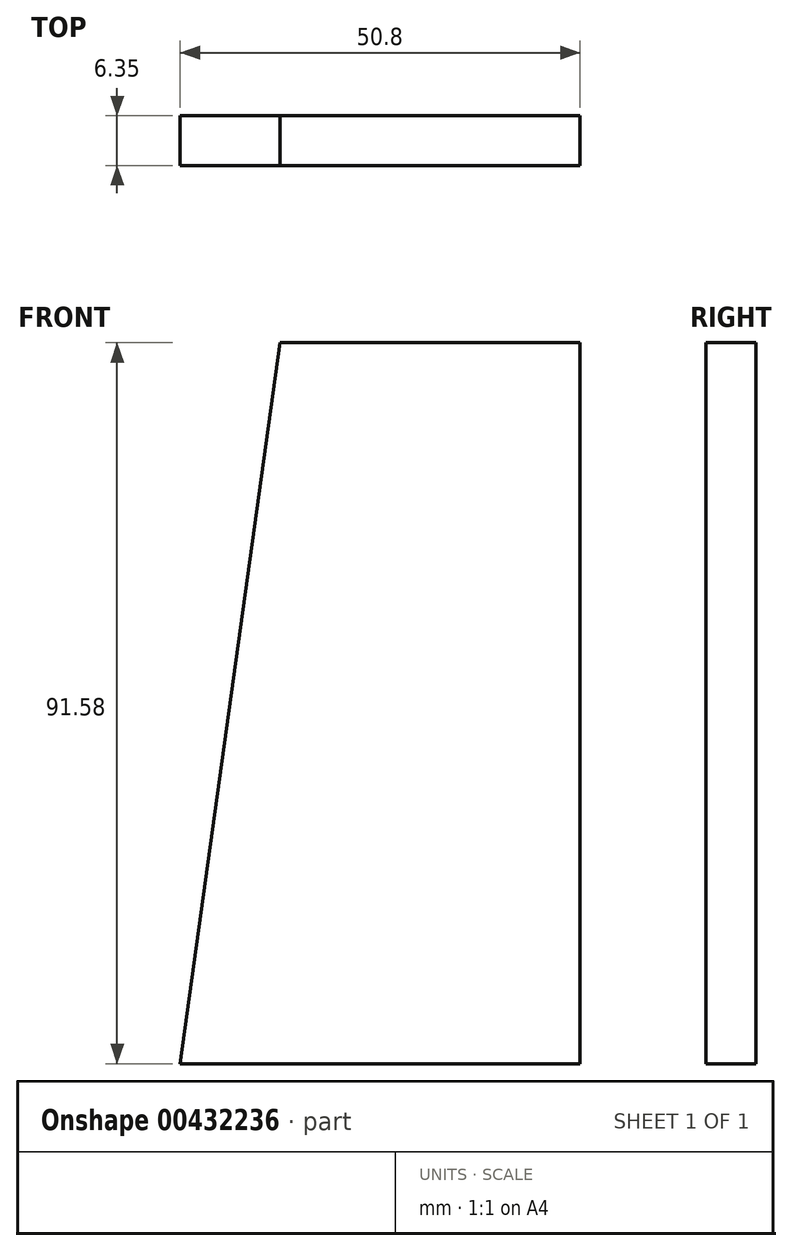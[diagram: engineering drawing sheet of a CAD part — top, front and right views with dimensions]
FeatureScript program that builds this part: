
annotation { "Feature Type Name" : "Feature", "Feature Type Description" : "" }
export const myFeature = defineFeature(function(context is Context, id is Id, definition is map)
    precondition{}
    {
        {
            var Q0;
            Q0=qCreatedBy(makeId("Front.planeOp"),FACE);
            var sketch = newSketch(context, id + "F0", { "sketchPlane" : qUnion([Q0])});
            skLineSegment(sketch, "E0", {"start": v(0, 0) * mm, "end": v(50.8, 0) * mm});
            skLineSegment(sketch, "E1", {"start": v(50.8, 0) * mm, "end": v(50.8, 91.58) * mm});
            skLineSegment(sketch, "E2", {"start": v(50.8, 91.58) * mm, "end": v(12.7, 91.58) * mm});
            skLineSegment(sketch, "E3", {"start": v(12.7, 91.58) * mm, "end": v(0, 0) * mm});
            skSolve(sketch);
        }
        {
            var Q0;
            Q0 = qSketchRegion(id + "F0", true);
            extrude(context, id + "F1", {"entities" : qUnion([Q0]), "depth" : 6.35 * mm});
        }
    });
